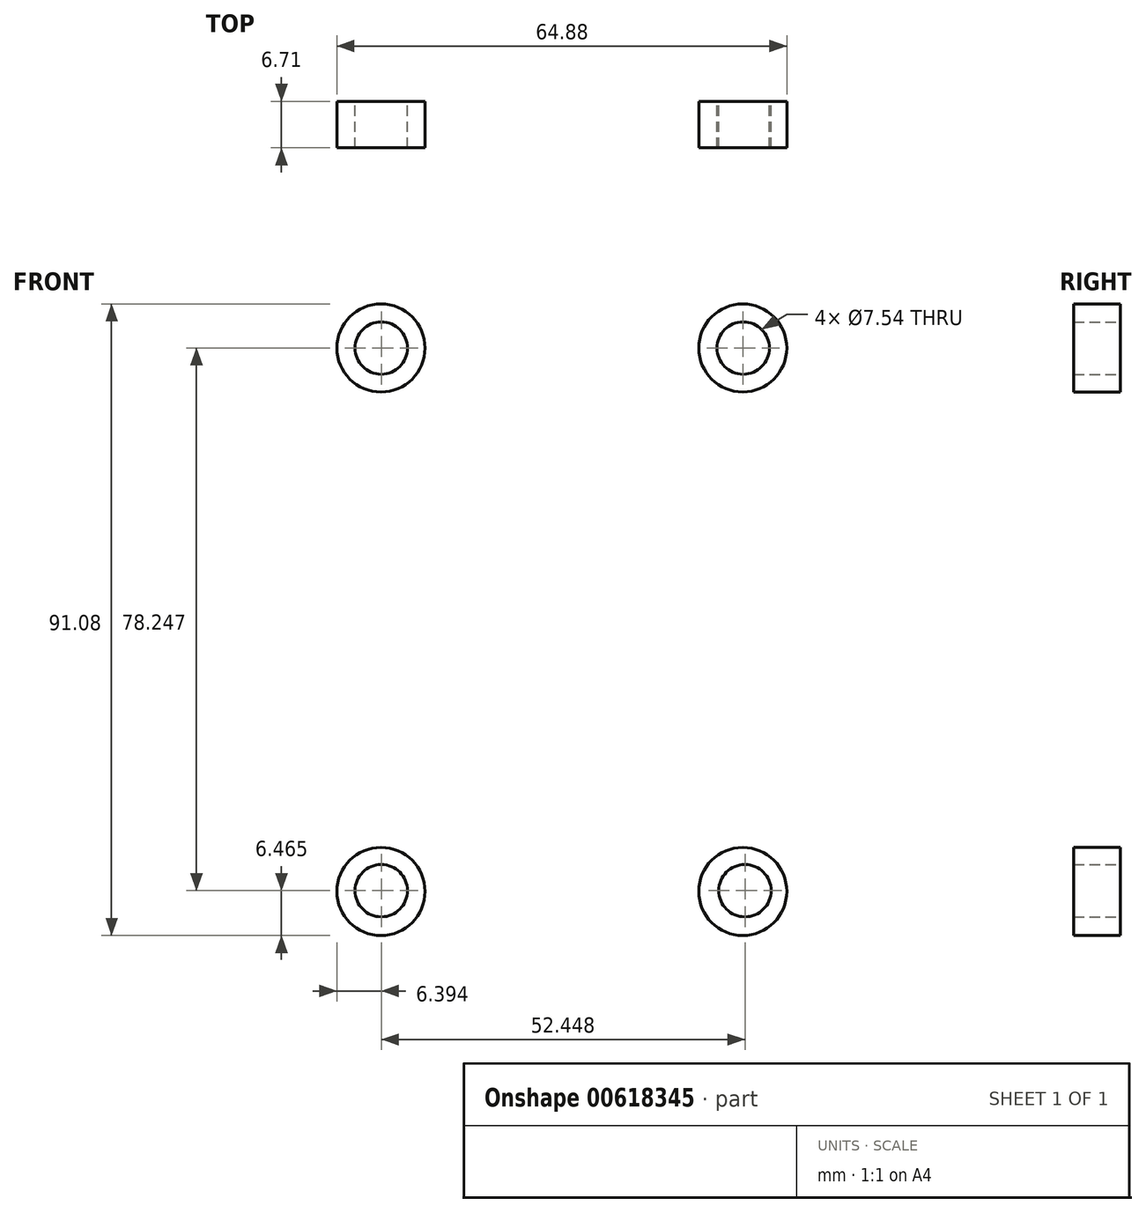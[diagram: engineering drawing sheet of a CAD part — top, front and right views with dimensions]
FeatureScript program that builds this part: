
annotation { "Feature Type Name" : "Feature", "Feature Type Description" : "" }
export const myFeature = defineFeature(function(context is Context, id is Id, definition is map)
    precondition{}
    {
        {
            var Q0;
            Q0=qCreatedBy(makeId("Front.planeOp"),FACE);
            var sketch = newSketch(context, id + "F0", { "sketchPlane" : qUnion([Q0])});
            skCircle(sketch, "E0", {"center": v(-26.09, 39.19) * mm, "radius": 6.35 * mm});
            skSolve(sketch);
        }
        {
            var Q0;
            Q0 = qSketchRegion(id + "F0", true);
            extrude(context, id + "F1", {"entities" : qUnion([Q0]), "depth" : 6.7 * mm, "offsetDistance" : 25.4 * mm});
        }
        {
            var Q0;
            Q0=makeQuery(id+"F1.opExtrude","SWEPT_BODY",BODY,{"disambiguationData":[OSD([sQuery(id+"F0.wireOp",EDGE,"E0")])]});
            var Q1;
            Q1=qCreatedBy(makeId("Right.planeOp"),FACE);
            mirror(context, id + "F2", {"entities" : qUnion([Q0]), "mirrorPlane" : qUnion([Q1])});
        }
        {
            var Q0;
            Q0=makeQuery(id+"F1.opExtrude","SWEPT_BODY",BODY,{"disambiguationData":[OSD([sQuery(id+"F0.wireOp",EDGE,"E0")])]});
            var Q1;
            Q1=qCreatedBy(makeId("Top.planeOp"),FACE);
            mirror(context, id + "F3", {"entities" : qUnion([Q0]), "mirrorPlane" : qUnion([Q1])});
        }
        {
            var Q0;
            Q0=makeQuery(id+"F3.opPattern","COPY",BODY,{"derivedFrom":makeQuery(id+"F1.opExtrude","SWEPT_BODY",BODY,{"disambiguationData":[OSD([sQuery(id+"F0.wireOp",EDGE,"E0")])]}),"instanceName":"1"});
            var Q1;
            Q1=qCreatedBy(makeId("Right.planeOp"),FACE);
            mirror(context, id + "F4", {"entities" : qUnion([Q0]), "mirrorPlane" : qUnion([Q1])});
        }
        {
            var Q0;
            Q0=qCreatedBy(makeId("Front.planeOp"),FACE);
            var sketch = newSketch(context, id + "F5", { "sketchPlane" : qUnion([Q0])});
            skCircle(sketch, "E1", {"center": v(-26.05, 39.17) * mm, "radius": 3.77 * mm});
            skCircle(sketch, "E2", {"center": v(26.15, 39.17) * mm, "radius": 3.77 * mm});
            skCircle(sketch, "E3", {"center": v(-26.05, -39.08) * mm, "radius": 3.77 * mm});
            skCircle(sketch, "E4", {"center": v(26.4, -39.08) * mm, "radius": 3.77 * mm});
            skSolve(sketch);
        }
        {
            var Q0;
            Q0 = qSketchRegion(id + "F5", true);
            extrude(context, id + "F6", {"entities" : qUnion([Q0]), "operationType" : NewBodyOperationType.REMOVE, "depth" : 15.24 * mm, "offsetDistance" : 25.4 * mm});
        }
    });
